# Revit family: BE_51258.1_de_DE
name_source: partatom
category: Lighting Fixtures
units: mm (PartAtom-declared; Revit-internal decimal feet)

## family parameters
Cut with Voids When Loaded = Yes
Host = Face
Light Source = Yes
Part Type = Normal
Room Calculation Point = Yes
Round Connector Dimension = Use Diameter
Shared = No

## types (1)
- BEGA_51258.1_K3
    AC/DC = AC/DC
    Aktualisierung = 2023-02-27T04:00:04
    Apparent Load = 0 VA
    BEGA_Dummy = No
    BEGA_IES = Yes
    BEGA_Intern = Yes
    BEGA_Intern_Konstruktion = Yes
    BEGA_Intern_an = Yes
    BEGA_Intern_aus = Yes
    Befestigungsabstand = 340 mm
    Befestigungsbohrung = Ø 4,5 mm
    Beschreibung_Sonderanfertigung = Hier können Sie Informationen zur Sonderanfertigung eintragen.
    Bestellnummer = 51258.1K3
    CE_Konformität = ja
    Color Filter = 16777215
    Default Elevation = 0 mm  [stored 0 ft]
    Description = Wandleuchte
    Dimming Lamp Color Temperature Shift = <None>
    Energieeffizienzklasse = LED A++ - A
    Farbtemperatur = 3000 K
    Farbwiedergabeindex = CRI > 90
    Frequenz = 0/50-60 Hz
    Gewicht = 2.0 kg
    LED_Modulbezeichnung = LED-1319/930
    Lamp = LED 13.5 W
    Lampenlichtstrom = 2100 lm
    Lastklassifizierung = Beleuchtung
    Lebensdauerkriterien = L70B50 @ 25 °C = 180000 h
    Leuchtenlichtstrom = 1407 lm
    Logo = <None>
    M_A = No
    M_G = No
    M_W = No
    Manufacturer = BEGA
    Material_06 = BEGA_Oberfläche_Edelstahl_gebürstet
    Material_14 = BEGA_Kunststoff_opal
    Material_22 = BEGA_Oberfläche_Aluminium_matt
    Material_34 = BEGA_Oberfläche_Samtweiss_matt
    Model = 51258.1K3
    Photometric Web File = BE_51258-1K3.ies
    Produktdatenblatt = https://cdn.bega.com
    Schutzart = IP 20
    Schutzklasse = I
    Sonderanfertigung = No
    Spannung = 240 V
    Tilt Angle = 0.00°
    URL = https://www.bega.com
    Umgebungstemperatur = 25 °C

note: [stored X ft] marks values corroborated as IEEE doubles in the binary element streams (Revit-internal decimal feet)
